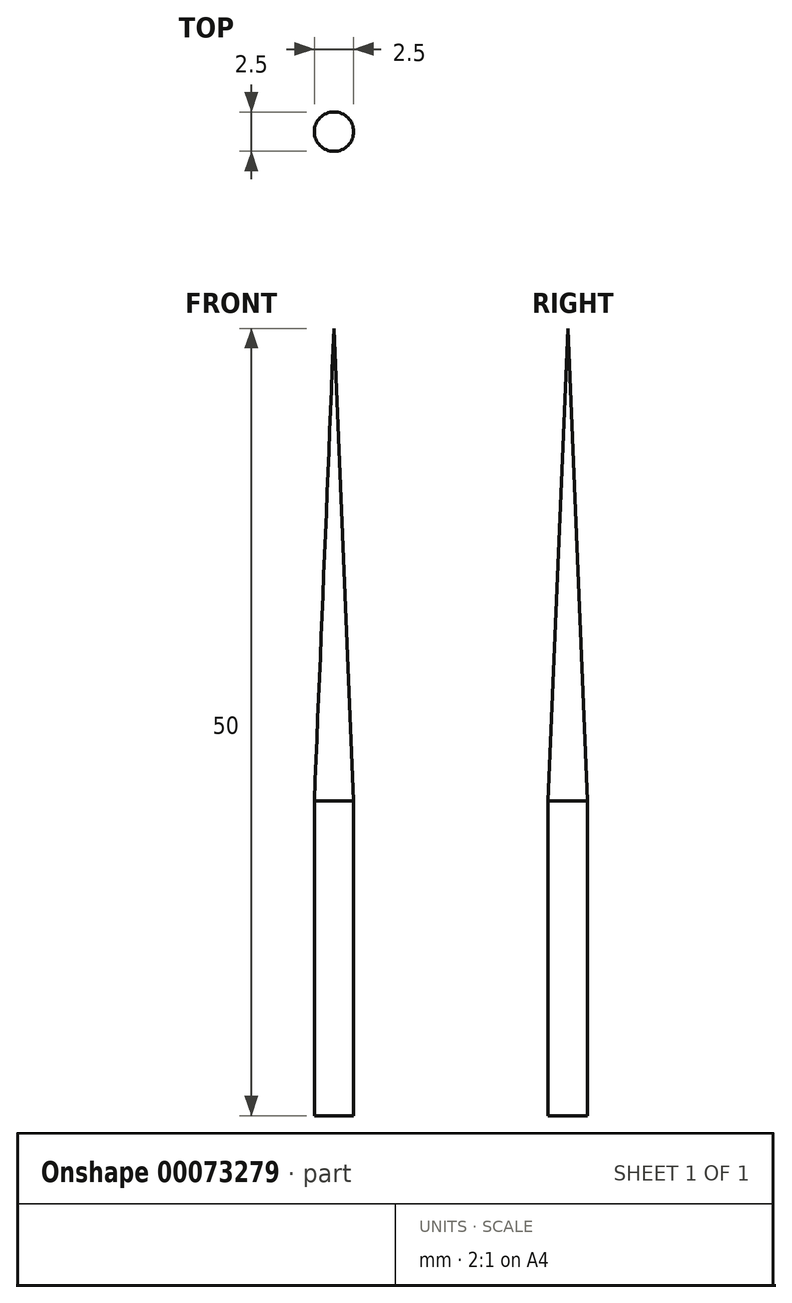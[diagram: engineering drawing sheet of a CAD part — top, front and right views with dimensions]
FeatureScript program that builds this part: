
annotation { "Feature Type Name" : "Feature", "Feature Type Description" : "" }
export const myFeature = defineFeature(function(context is Context, id is Id, definition is map)
    precondition{}
    {
        {
            var Q0;
            Q0=qCreatedBy(makeId("Front.planeOp"),FACE);
            var sketch = newSketch(context, id + "F0", { "sketchPlane" : qUnion([Q0])});
            skLineSegment(sketch, "E0", {"start": v(-1.25, 0) * mm, "end": v(-1.25, 20) * mm});
            skLineSegment(sketch, "E1", {"start": v(-1.25, 20) * mm, "end": v(0, 50) * mm});
            skLineSegment(sketch, "E2", {"start": v(0, -13.71) * mm, "end": v(0, 63.37) * mm, "construction": true});
            skLineSegment(sketch, "E3", {"start": v(-1.25, 0) * mm, "end": v(0, 0) * mm});
            skLineSegment(sketch, "E4", {"start": v(0, 0) * mm, "end": v(0, 50) * mm});
            skSolve(sketch);
        }
        {
            var Q0;
            Q0=makeQuery(id+"F0.imprint","IMPRINT",FACE,{"disambiguationData":[TD([[makeQuery(id+"F0.imprint","IMPRINT",EDGE,{"derivedFrom":sQuery(id+"F0.wireOp",EDGE,"E0")}),-1.0]])]});
            var Q1;
            Q1=sQuery(id+"F0.wireOp",EDGE,"E2");
            revolve(context, id + "F1", {"entities" : qUnion([Q0]), "axis" : qUnion([Q1]), "revolveType" : RevolveType.FULL});
        }
    });
